# Revit family: CBCOMTYP001
name_source: partatom
category: Furniture
units: mm (PartAtom-declared; Revit-internal decimal feet)

## family parameters
Always vertical = Yes
Cut with Voids When Loaded = No
OmniClass Number = 23.40.20.00
OmniClass Title = General Furniture and Specialties
Render Appearance Source = Family Geometry
Room Calculation Point = No
Shared = No
Work Plane-Based = No

## types (1)
- CBCOMTYP001
    Cost = 65760 $
    Default Elevation = 0 mm  [stored 0 ft]
    Description = 4 x Grafton Side Chair Black Mesh Back/fabric Choice Seat, 4 x Natick Grey Configurable Task Chair, 4 x Calibrate Cantilevered Spine Surface 18d x 60w KNIFE Edge, 2 x CB Community EP Mid Mount 24d x 66h x 29h, 1 x CB Community Infeed Base Support 24d x 6w x 21h, 2 x CB Community Spine Pwr 2 Side 90w x 24d, 2 x CB Community Spine Hutch D Open LH 72w x 18d x 36h x 08h, 1 x CB Community Spine Hutch K 36w x 24d x 37h, 4 x CB Community PET Tackboard For 36hx72w Hutch D 08h Cubby, 4 x Duplex Outlet - Line 1, 4 x Duplex Outlet - Line 2, 1 x 79 in. Electrical Jumper (Pt 60 &amp; Vt 64), 1 x Side Mounted Base Infeed - 72L - 8 Wire, 4 Circuit, 1 x Pack fee per Chair is less than multiple of 3, 2 x CBX Combo B/F Ped Left/Bookcase Right 18D x 21H x 72W, 2 x CBX Combo B/F Ped Right/Bookcase Left 18D x 21H x 72W, 4 x Calibrate Fixed Runoff 30 x 60 KNIFE Tapered Leg with Glides
    Exported From CET Designer = Yes
    Manufacturer = AIS
    Model = 4060C
    Show CBCOMTYP001 = Yes
    VisibilityIndex = 0

note: [stored X ft] marks values corroborated as IEEE doubles in the binary element streams (Revit-internal decimal feet)

## geometry (parser evidence)
native form markers: Sweep x2
no freeform markers — native parametric forms only
